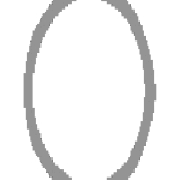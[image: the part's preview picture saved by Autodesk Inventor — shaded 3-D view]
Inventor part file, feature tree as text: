
AUTODESK INVENTOR PART (.ipt)
format: ipt  version: 2021 (Build 250183000, 183)  size: 109,056 bytes
history: native  units: in
note: dims shown in document units (in); Inventor stores cm internally (conversion verified against a paired STEP export)
features: other x4, sketch x3, plane x1
ambient origin geometry x8: Origin, YZ Plane, XZ Plane, XY Plane, X Axis, Y Axis, Z Axis, Center Point
bodies: Solid1 (feature_tree), Body (feature_tree)
feature tree (8):
  other  "Driven Length"
  other  "Frame Generator"
  other  "Start Plane"
  other  "End Plane"
  sketch  "Sketch"  dims[d2=19.6468in d4=-0.0in d5=19.6468in d6=0.12in d7=0.0in d8=90.0deg d9=19.6468in]
  sketch  "Sketch2"  dims[d0=1.0in]
  plane  "Work Plane3"
  sketch  "Sketch3"  dims[d1=0.065in]
